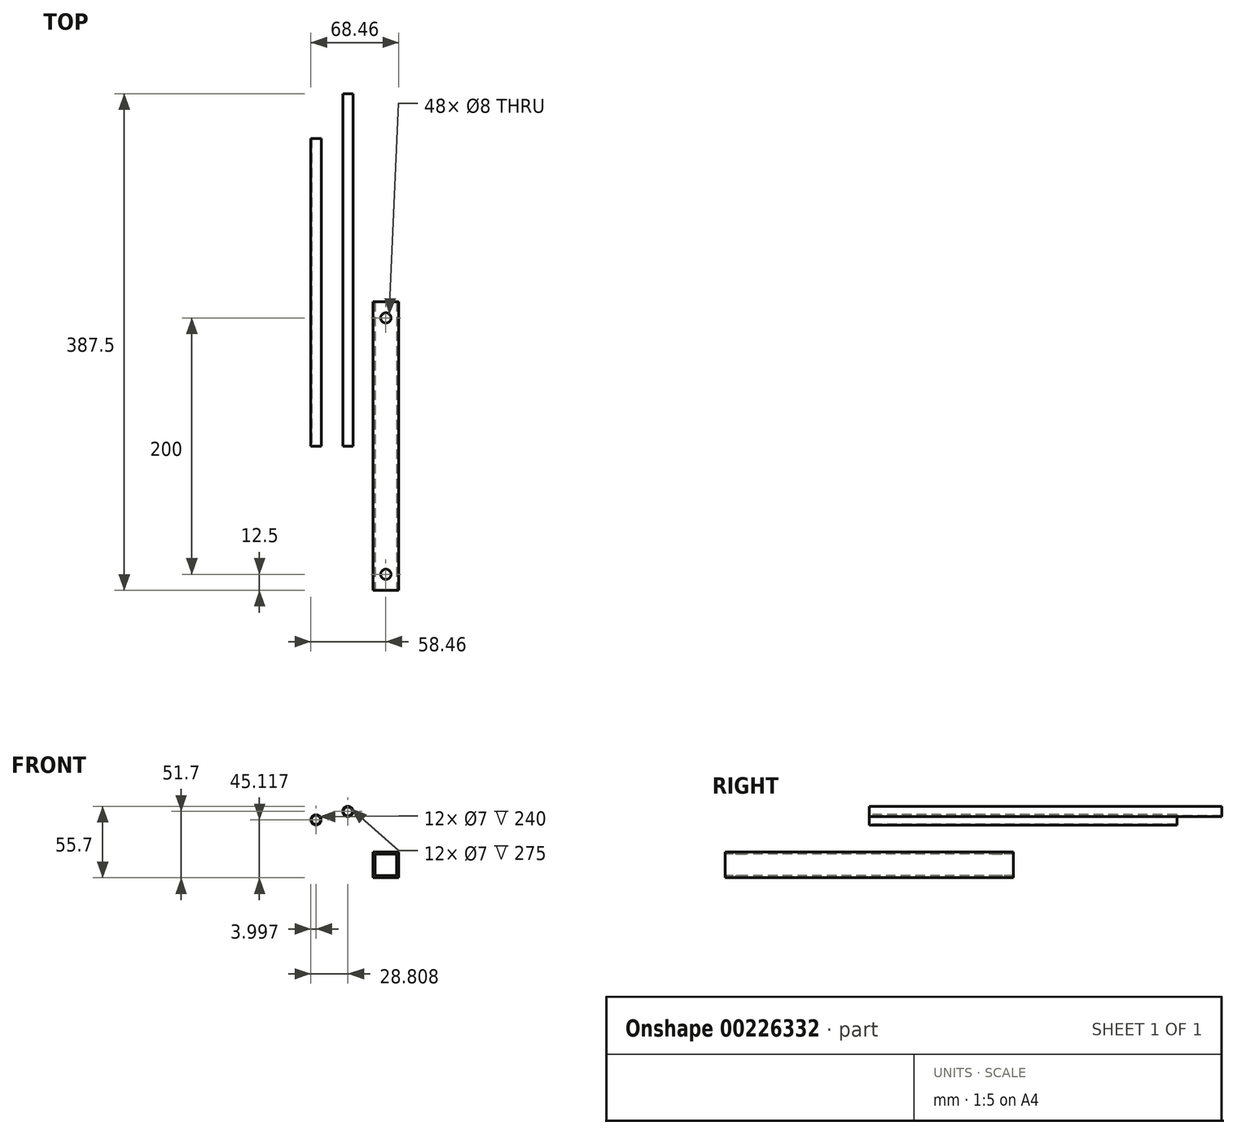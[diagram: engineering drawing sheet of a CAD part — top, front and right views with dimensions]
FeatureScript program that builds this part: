
annotation { "Feature Type Name" : "Feature", "Feature Type Description" : "" }
export const myFeature = defineFeature(function(context is Context, id is Id, definition is map)
    precondition{}
    {
        {
            var Q0;
            Q0=qCreatedBy(makeId("Top.planeOp"),FACE);
            var sketch = newSketch(context, id + "F0", { "sketchPlane" : qUnion([Q0])});
            skLineSegment(sketch, "E0.bottom", {"start": v(10, -112.5) * mm, "end": v(-10, -112.5) * mm});
            skLineSegment(sketch, "E0.top", {"start": v(10, 112.5) * mm, "end": v(-10, 112.5) * mm});
            skLineSegment(sketch, "E0.left", {"start": v(10, -112.5) * mm, "end": v(10, 112.5) * mm});
            skLineSegment(sketch, "E0.right", {"start": v(-10, -112.5) * mm, "end": v(-10, 112.5) * mm});
            skPoint(sketch, "E0.middle", {"position": v(0, 0) * mm});
            skSolve(sketch);
        }
        {
            var Q0;
            Q0 = qSketchRegion(id + "F0", true);
            extrude(context, id + "F1", {"entities" : qUnion([Q0]), "depth" : 20 * mm});
        }
        {
            var Q0;
            Q0=makeQuery(id+"F1.opExtrude","SWEPT_FACE",FACE,{"disambiguationData":[OSD([sQuery(id+"F0.wireOp",EDGE,"E0.bottom")])]});
            var sketch = newSketch(context, id + "F2", { "sketchPlane" : qUnion([Q0])});
            skLineSegment(sketch, "E1", {"start": v(10, 20) * mm, "end": v(-10, 0) * mm});
            skLineSegment(sketch, "E2.bottom", {"start": v(8.5, 1.5) * mm, "end": v(-8.5, 1.5) * mm});
            skLineSegment(sketch, "E2.top", {"start": v(8.5, 18.5) * mm, "end": v(-8.5, 18.5) * mm});
            skLineSegment(sketch, "E2.left", {"start": v(8.5, 1.5) * mm, "end": v(8.5, 18.5) * mm});
            skLineSegment(sketch, "E2.right", {"start": v(-8.5, 1.5) * mm, "end": v(-8.5, 18.5) * mm});
            skPoint(sketch, "E2.middle", {"position": v(0, 10) * mm});
            skSolve(sketch);
        }
        {
            var Q0;
            Q0 = qSketchRegion(id + "F2", true);
            extrude(context, id + "F3", {"entities" : qUnion([Q0]), "operationType" : NewBodyOperationType.REMOVE, "oppositeDirection" : true, "depth" : 225 * mm});
        }
        {
            var Q0;
            Q0=makeQuery(id+"F1.opExtrude","CAP_FACE",FACE,{"disambiguationData":[OSD([sQuery(id+"F0.wireOp",EDGE,"E0.bottom"),sQuery(id+"F0.wireOp",EDGE,"E0.top"),sQuery(id+"F0.wireOp",EDGE,"E0.left"),sQuery(id+"F0.wireOp",EDGE,"E0.right")])],"isStart":false});
            var sketch = newSketch(context, id + "F4", { "sketchPlane" : qUnion([Q0])});
            skLineSegment(sketch, "E3.bottom", {"start": v(-10, 112.5) * mm, "end": v(10, 112.5) * mm});
            skLineSegment(sketch, "E3.top", {"start": v(-10, 87.5) * mm, "end": v(10, 87.5) * mm});
            skLineSegment(sketch, "E3.left", {"start": v(-10, 112.5) * mm, "end": v(-10, 87.5) * mm});
            skLineSegment(sketch, "E3.right", {"start": v(10, 112.5) * mm, "end": v(10, 87.5) * mm});
            skLineSegment(sketch, "E4", {"start": v(-10, 112.5) * mm, "end": v(10, 87.5) * mm});
            skCircle(sketch, "E5", {"center": v(0, 100) * mm, "radius": 4 * mm});
            skLineSegment(sketch, "E6.bottom", {"start": v(-10, -112.5) * mm, "end": v(10, -112.5) * mm});
            skLineSegment(sketch, "E6.top", {"start": v(-10, -87.5) * mm, "end": v(10, -87.5) * mm});
            skLineSegment(sketch, "E6.left", {"start": v(-10, -112.5) * mm, "end": v(-10, -87.5) * mm});
            skLineSegment(sketch, "E6.right", {"start": v(10, -112.5) * mm, "end": v(10, -87.5) * mm});
            skLineSegment(sketch, "E7", {"start": v(-10, -87.5) * mm, "end": v(10, -112.5) * mm});
            skCircle(sketch, "E8", {"center": v(0, -100) * mm, "radius": 4 * mm});
            skSolve(sketch);
        }
        {
            var Q0;
            Q0=sQuery(id+"F4.wireOp",VERTEX,"E8.center");
            var Q1;
            Q1=sQuery(id+"F4.wireOp",VERTEX,"E5.center");
            var Q2;
            Q2=makeQuery(id+"F1.opExtrude","SWEPT_BODY",BODY,{"disambiguationData":[OSD([sQuery(id+"F0.wireOp",EDGE,"E0.bottom"),sQuery(id+"F0.wireOp",EDGE,"E0.top"),sQuery(id+"F0.wireOp",EDGE,"E0.left"),sQuery(id+"F0.wireOp",EDGE,"E0.right")])]});
            hole(context, id + "F5", {"style" : HoleStyle.SIMPLE, "endStyle" : HoleEndStyle.BLIND, "holeDiameter" : 8 * mm, "holeDepth" : 450 * mm, "locations" : qUnion([Q0, Q1]), "scope" : qUnion([Q2])});
        }
        {
            var Q0;
            Q0=qCreatedBy(makeId("Front.planeOp"),FACE);
            var sketch = newSketch(context, id + "F6", { "sketchPlane" : qUnion([Q0])});
            skCircle(sketch, "E9", {"center": v(-54.46, 45.12) * mm, "radius": 4 * mm});
            skCircle(sketch, "E10", {"center": v(-54.46, 45.12) * mm, "radius": 3.5 * mm});
            skSolve(sketch);
        }
        {
            var Q0;
            Q0=makeQuery(id+"F6.imprint","IMPRINT",FACE,{"disambiguationData":[TD([[makeQuery(id+"F6.imprint","IMPRINT",EDGE,{"derivedFrom":sQuery(id+"F6.wireOp",EDGE,"E9")}),1.0]])]});
            extrude(context, id + "F7", {"entities" : qUnion([Q0]), "oppositeDirection" : true, "depth" : 240 * mm});
        }
        {
            var Q0;
            Q0=qCreatedBy(makeId("Front.planeOp"),FACE);
            var sketch = newSketch(context, id + "F8", { "sketchPlane" : qUnion([Q0])});
            skCircle(sketch, "E11", {"center": v(-29.65, 51.7) * mm, "radius": 4 * mm});
            skCircle(sketch, "E12", {"center": v(-29.65, 51.7) * mm, "radius": 3.5 * mm});
            skSolve(sketch);
        }
        {
            var Q0;
            Q0=makeQuery(id+"F8.imprint","IMPRINT",FACE,{"disambiguationData":[TD([[makeQuery(id+"F8.imprint","IMPRINT",EDGE,{"derivedFrom":sQuery(id+"F8.wireOp",EDGE,"E11")}),1.0]])]});
            extrude(context, id + "F9", {"entities" : qUnion([Q0]), "oppositeDirection" : true, "depth" : 275 * mm});
        }
    });
